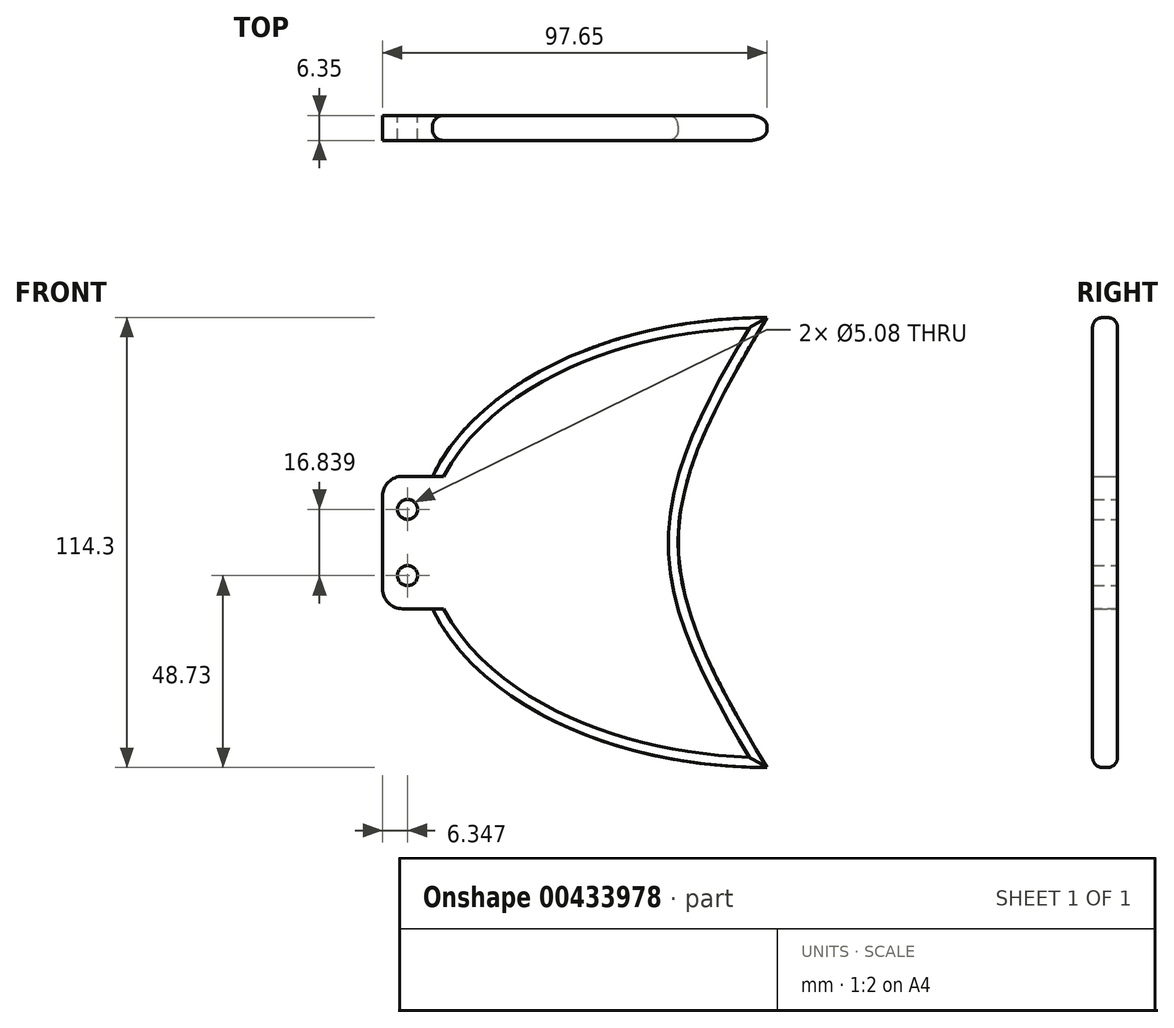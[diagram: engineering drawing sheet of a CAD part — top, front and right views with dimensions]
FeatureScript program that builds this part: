
annotation { "Feature Type Name" : "Feature", "Feature Type Description" : "" }
export const myFeature = defineFeature(function(context is Context, id is Id, definition is map)
    precondition{}
    {
        {
            var Q0;
            Q0=qCreatedBy(makeId("Front.planeOp"),FACE);
            var sketch = newSketch(context, id + "F0", { "sketchPlane" : qUnion([Q0])});
            skEllipticalArc(sketch, "E0", {});
            skFitSpline(sketch, "E1", {"points": [v(0, 57.15) * mm, v(-22.58, 0) * mm, v(0, -57.15) * mm], "startDerivative": vector(-67.73, -114.3) * mm, "endDerivative": vector(67.73, -114.3) * mm});
            skLineSegment(sketch, "E2", {"start": v(-22.58, 0) * mm, "end": v(-88.9, 0) * mm, "construction": true});
            skLineSegment(sketch, "E3", {"start": v(-84.95, -16.84) * mm, "end": v(-97.65, -16.84) * mm});
            skLineSegment(sketch, "E4", {"start": v(-97.65, -16.84) * mm, "end": v(-97.65, 16.84) * mm});
            skLineSegment(sketch, "E5", {"start": v(-97.65, 16.84) * mm, "end": v(-84.95, 16.84) * mm});
            skEllipticalArc(sketch, "E6.trimOffspring", {});
            skLineSegment(sketch, "E7", {"start": v(-84.95, 0) * mm, "end": v(-97.65, 0) * mm, "construction": true});
            skLineSegment(sketch, "E8", {"start": v(-97.65, 16.84) * mm, "end": v(-97.65, 0) * mm});
            skLineSegment(sketch, "E9", {"start": v(-97.65, -16.84) * mm, "end": v(-97.65, 0) * mm});
            skCircle(sketch, "E10", {"center": v(-91.3, 8.42) * mm, "radius": 2.54 * mm});
            skPoint(sketch, "E10.centerSnap0", {"position": v(-97.65, 8.42) * mm});
            skPoint(sketch, "E10.centerSnap1", {"position": v(-91.3, 16.84) * mm});
            skCircle(sketch, "E11", {"center": v(-91.3, -8.42) * mm, "radius": 2.54 * mm});
            skPoint(sketch, "E11.centerSnap0", {"position": v(-91.3, 0) * mm});
            skPoint(sketch, "E11.centerSnap1", {"position": v(-97.65, -8.42) * mm});
            const initialGuessF0  = {"E0": [0, 0, 1, 0, 0.0889, 0.05715, 1.5707963267948966, 2.8425012953945505], "E6.trimOffspring": [0, 0, 1, 0, 0.0889, 0.05715, 3.4406840117850344, 4.71238898038469]};
            skSetInitialGuess(sketch, initialGuessF0);
            skSolve(sketch);
        }
        {
            var Q0;
            Q0=makeQuery(id+"F0.imprint","IMPRINT",FACE,{"disambiguationData":[TD([[makeQuery(id+"F0.imprint","IMPRINT",EDGE,{"derivedFrom":sQuery(id+"F0.wireOp",EDGE,"E0")}),1.0]])]});
            extrude(context, id + "F1", {"entities" : qUnion([Q0]), "depth" : 6.35 * mm});
        }
        {
            var Q0;
            Q0=makeQuery(id+"F1.opExtrude","CAP_EDGE",EDGE,{"disambiguationData":[OSD([sQuery(id+"F0.wireOp",EDGE,"E0")])],"isStart":false});
            var Q1;
            Q1=makeQuery(id+"F1.opExtrude","CAP_EDGE",EDGE,{"disambiguationData":[OSD([sQuery(id+"F0.wireOp",EDGE,"E0")])],"isStart":true});
            var Q2;
            Q2=makeQuery(id+"F1.opExtrude","CAP_EDGE",EDGE,{"disambiguationData":[OSD([sQuery(id+"F0.wireOp",EDGE,"E6.trimOffspring")])],"isStart":false});
            var Q3;
            Q3=makeQuery(id+"F1.opExtrude","CAP_EDGE",EDGE,{"disambiguationData":[OSD([sQuery(id+"F0.wireOp",EDGE,"E6.trimOffspring")])],"isStart":true});
            var Q4;
            Q4=makeQuery(id+"F1.opExtrude","CAP_EDGE",EDGE,{"disambiguationData":[OSD([sQuery(id+"F0.wireOp",EDGE,"E1")])],"isStart":false});
            var Q5;
            Q5=makeQuery(id+"F1.opExtrude","CAP_EDGE",EDGE,{"disambiguationData":[OSD([sQuery(id+"F0.wireOp",EDGE,"E1")])],"isStart":true});
            fillet(context, id + "F2", {"entities" : qUnion([Q0, Q1, Q2, Q3, Q4, Q5]), "radius" : 2.54 * mm, "tangentPropagation" : true, "allowEdgeOverflow" : false});
        }
        {
            var Q0;
            Q0=makeQuery(id+"F1.opExtrude","SWEPT_EDGE",EDGE,{"disambiguationData":[OSD([sQuery(id+"F0.wireOp",EDGE,"E4"),sQuery(id+"F0.wireOp",EDGE,"E5")])]});
            var Q1;
            Q1=makeQuery(id+"F1.opExtrude","SWEPT_EDGE",EDGE,{"disambiguationData":[OSD([sQuery(id+"F0.wireOp",EDGE,"E3"),sQuery(id+"F0.wireOp",EDGE,"E4")])]});
            fillet(context, id + "F3", {"entities" : qUnion([Q0, Q1]), "radius" : 5.08 * mm, "tangentPropagation" : true, "allowEdgeOverflow" : false});
        }
    });
